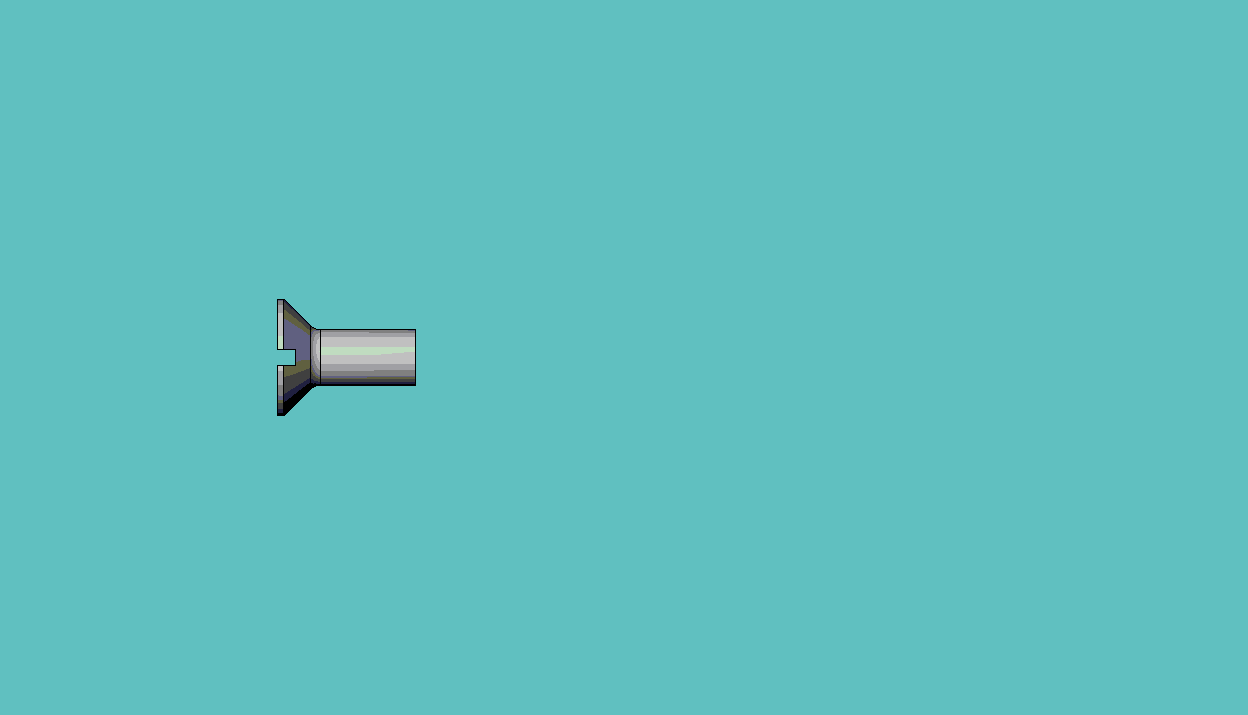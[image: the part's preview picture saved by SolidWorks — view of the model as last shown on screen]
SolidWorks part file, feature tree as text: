
SOLIDWORKS PART (.sldprt)
format: sldprt  version: not decoded by parser v0  size: 143,872 bytes
history: native  units: mm
features: plane x3, sketch x3, material x1, revolve x1, thread x1, cut_extrude x1, fillet x1, cut_revolve x1, pattern_linear x1 (+10 scaffold rows collapsed; 1 parser-record rows omitted)
feature tree (24):
  scaffold x10  (default folders/planes/origin — collapsed)
  material  "Material <not specified>"
  plane  "Plane1"
  plane  "Plane2"
  plane  "Plane3"
  parser-record x1  (decoder bookkeeping rows leaked as tree rows — omitted from the tree; the rows remain in map.json)
  revolve  "Base-Revolve"  [1 undecoded]
  sketch  "BodySke"  dims[c1.Diameter=4.0mm c1.D2=76.2mm c1.D3=5.842mm c1.D4=~18.513272mm c2.D4=82.0deg c2.D5=~19.681746mm c3.D4=19.3548mm c3.D5=~7.740726mm c4.D5=~80.148096deg c4.Length=10.0mm c4.Head_ht=2.7mm c4.Head_dia=8.4mm c5.D5=~8.373577mm c5.Head_ang=90.0deg c5.D6=0.5mm c5.D7=88.9mm c5.Advance=0.7mm c5.Thread_nom=10.0mm c5.Thread_lim=30.6705mm]
  thread  "ThreadCosmetic"  Diameter=6.6mm Thread_length=6.6mm Thread_minor=3.22mm  [1 undecoded]
  cut_extrude  "Slot"  [1 undecoded]
  sketch  "Sketch2"  dims[Slot_width=1.2mm D1=0.6mm D2=8.4mm D3=4.2mm Slot_depth=1.3mm]
  fillet  "Fillet1"  Radius=1mm
  sketch  "ThdSchSke"  dims[c1.Thread_minor=~1.03886mm c1.Diameter=~1.413535mm c1.Start=~0.988134mm c1.D4=~4.446753mm c1.Vee=60.0deg c2.Thread_minor=~1.03886mm c2.Start=~2.540025mm c2.D1=~0.108159mm c2.D2=~0.108159mm c3.D1=~0.216319mm c3.SideAngle=55.0deg c3.D2=~0.216319mm c3.VeeAngle=70.0deg c3.Thread_minor=3.22mm c3.Overcut=5.0mm c3.Diameter=4.0mm c3.D6=~8.326268mm c4.D1=~8.326268mm c5.D1=90.0deg c5.Start=11.1125mm c6.Start=~44.450025mm c7.Start=~3.400001mm]
  cut_revolve  "ThreadSchematic"  Angle=360deg
  pattern_linear  "ThdSchPat"  Count1=11 Count2=1 Spacing1=0.66mm Spacing2=50mm Num_threads=11 Advance=0.66mm CopiedFlag=1
decode coverage: 7 of 9 modeling features carry decoded parameters
note: ~ marks probable driven/reference dimensions
note: 3 parameter values undecoded
note: suppression state not decoded; provenance and decode notes live in map.json
